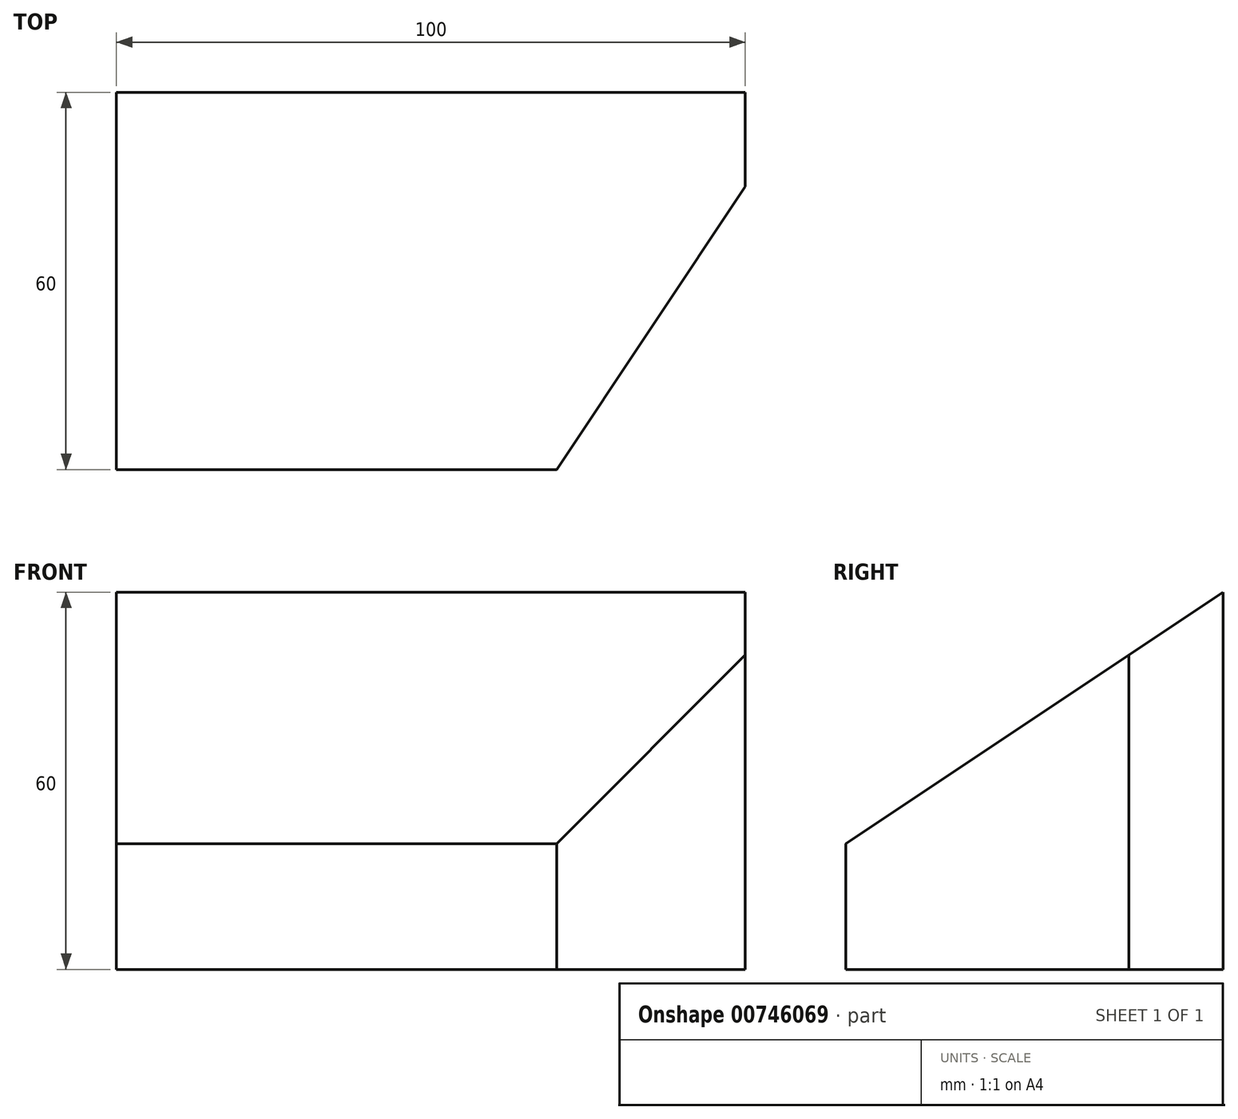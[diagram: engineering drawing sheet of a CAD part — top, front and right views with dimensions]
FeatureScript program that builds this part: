
annotation { "Feature Type Name" : "Feature", "Feature Type Description" : "" }
export const myFeature = defineFeature(function(context is Context, id is Id, definition is map)
    precondition{}
    {
        {
            var Q0;
            Q0=qCreatedBy(makeId("Top.planeOp"),FACE);
            var sketch = newSketch(context, id + "F0", { "sketchPlane" : qUnion([Q0])});
            skLineSegment(sketch, "E0.bottom", {"start": v(0, 0) * mm, "end": v(100, 0) * mm});
            skLineSegment(sketch, "E0.top", {"start": v(0, 60) * mm, "end": v(100, 60) * mm});
            skLineSegment(sketch, "E0.left", {"start": v(0, 0) * mm, "end": v(0, 60) * mm});
            skLineSegment(sketch, "E0.right", {"start": v(100, 0) * mm, "end": v(100, 60) * mm});
            skSolve(sketch);
        }
        {
            var Q0;
            Q0 = qSketchRegion(id + "F0", true);
            extrude(context, id + "F1", {"entities" : qUnion([Q0]), "depth" : 60 * mm, "offsetDistance" : 25 * mm});
        }
        {
            var Q0;
            Q0=makeQuery(id+"F1.opExtrude","CAP_FACE",FACE,{"disambiguationData":[OSD([sQuery(id+"F0.wireOp",EDGE,"E0.bottom"),sQuery(id+"F0.wireOp",EDGE,"E0.top"),sQuery(id+"F0.wireOp",EDGE,"E0.left"),sQuery(id+"F0.wireOp",EDGE,"E0.right")])],"isStart":false});
            var sketch = newSketch(context, id + "F2", { "sketchPlane" : qUnion([Q0])});
            skLineSegment(sketch, "E1", {"start": v(70, 0) * mm, "end": v(100, 45) * mm});
            skSolve(sketch);
        }
        {
            var Q0;
            Q0 = qSketchRegion(id + "F2", true);
            var Q1;
            {var subQ0=sQuery(id+"F2.wireOp",EDGE,"E1");Q1=makeQuery(id+"F2.imprint","IMPRINT",FACE,{"disambiguationData":[TD([[makeQuery(id+"F2.imprint","IMPRINT",EDGE,{"derivedFrom":subQ0}),-1.0]])]});}
            extrude(context, id + "F3", {"entities" : qUnion([Q0, Q1]), "operationType" : NewBodyOperationType.REMOVE, "endBound" : BoundingType.THROUGH_ALL, "oppositeDirection" : true, "depth" : 25 * mm, "offsetDistance" : 25 * mm});
        }
        {
            var Q0;
            Q0=makeQuery(id+"F1.opExtrude","SWEPT_FACE",FACE,{"disambiguationData":[OSD([sQuery(id+"F0.wireOp",EDGE,"E0.left")])]});
            var sketch = newSketch(context, id + "F4", { "sketchPlane" : qUnion([Q0])});
            skLineSegment(sketch, "E2", {"start": v(-60, 60) * mm, "end": v(0, 20) * mm});
            skSolve(sketch);
        }
        {
            var Q0;
            Q0 = qSketchRegion(id + "F4", true);
            var Q1;
            {var subQ0=sQuery(id+"F4.wireOp",EDGE,"E2");Q1=makeQuery(id+"F4.imprint","IMPRINT",FACE,{"disambiguationData":[TD([[makeQuery(id+"F4.imprint","IMPRINT",EDGE,{"derivedFrom":subQ0}),1.0]])]});}
            extrude(context, id + "F5", {"entities" : qUnion([Q0, Q1]), "operationType" : NewBodyOperationType.REMOVE, "endBound" : BoundingType.THROUGH_ALL, "oppositeDirection" : true, "depth" : 25 * mm, "offsetDistance" : 25 * mm});
        }
    });
